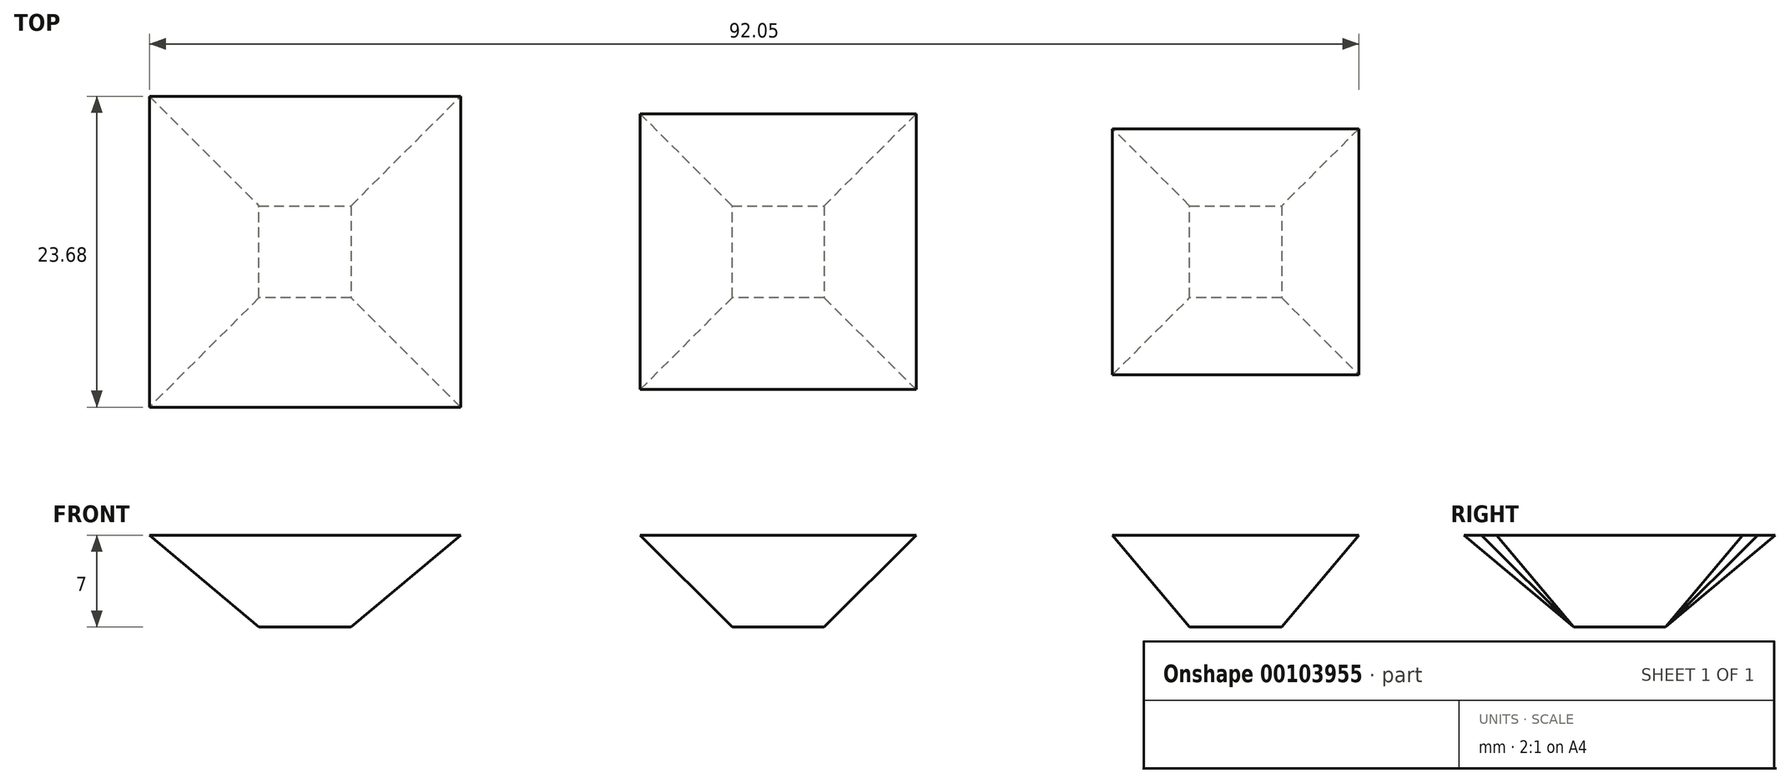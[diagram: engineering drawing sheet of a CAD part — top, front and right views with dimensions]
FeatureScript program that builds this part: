
annotation { "Feature Type Name" : "Feature", "Feature Type Description" : "" }
export const myFeature = defineFeature(function(context is Context, id is Id, definition is map)
    precondition{}
    {
        {
            var Q0;
            Q0=qCreatedBy(makeId("Top.planeOp"),FACE);
            var sketch = newSketch(context, id + "F0", { "sketchPlane" : qUnion([Q0])});
            skLineSegment(sketch, "E0.bottom", {"start": v(3.5, -3.5) * mm, "end": v(-3.5, -3.5) * mm});
            skLineSegment(sketch, "E0.top", {"start": v(3.5, 3.5) * mm, "end": v(-3.5, 3.5) * mm});
            skLineSegment(sketch, "E0.left", {"start": v(3.5, -3.5) * mm, "end": v(3.5, 3.5) * mm});
            skLineSegment(sketch, "E0.right", {"start": v(-3.5, -3.5) * mm, "end": v(-3.5, 3.5) * mm});
            skPoint(sketch, "E0.middle", {"position": v(0, 0) * mm});
            skSolve(sketch);
        }
        {
            var Q0;
            Q0 = qSketchRegion(id + "F0", true);
            extrude(context, id + "F1", {"entities" : qUnion([Q0]), "depth" : 7 * mm, "hasDraft" : true, "draftAngle" : 45 * degree});
        }
        {
            var Q0;
            Q0=qCreatedBy(makeId("Top.planeOp"),FACE);
            var sketch = newSketch(context, id + "F2", { "sketchPlane" : qUnion([Q0])});
            skLineSegment(sketch, "E1.bottom", {"start": v(-32.5, 3.5) * mm, "end": v(-39.5, 3.5) * mm});
            skLineSegment(sketch, "E1.top", {"start": v(-32.5, -3.5) * mm, "end": v(-39.5, -3.5) * mm});
            skLineSegment(sketch, "E1.left", {"start": v(-32.5, 3.5) * mm, "end": v(-32.5, -3.5) * mm});
            skLineSegment(sketch, "E1.right", {"start": v(-39.5, 3.5) * mm, "end": v(-39.5, -3.5) * mm});
            skPoint(sketch, "E1.middle", {"position": v(-36, 0) * mm});
            skSolve(sketch);
        }
        {
            var Q0;
            Q0 = qSketchRegion(id + "F2", true);
            extrude(context, id + "F3", {"entities" : qUnion([Q0]), "depth" : 7 * mm, "hasDraft" : true, "draftAngle" : 50 * degree});
        }
        {
            var Q0;
            Q0=qCreatedBy(makeId("Top.planeOp"),FACE);
            var sketch = newSketch(context, id + "F4", { "sketchPlane" : qUnion([Q0])});
            skLineSegment(sketch, "E2.bottom", {"start": v(38.32, -3.5) * mm, "end": v(31.32, -3.5) * mm});
            skLineSegment(sketch, "E2.top", {"start": v(38.32, 3.5) * mm, "end": v(31.32, 3.5) * mm});
            skLineSegment(sketch, "E2.left", {"start": v(38.32, -3.5) * mm, "end": v(38.32, 3.5) * mm});
            skLineSegment(sketch, "E2.right", {"start": v(31.32, -3.5) * mm, "end": v(31.32, 3.5) * mm});
            skPoint(sketch, "E2.middle", {"position": v(34.82, 0) * mm});
            skSolve(sketch);
        }
        {
            var Q0;
            Q0 = qSketchRegion(id + "F4", true);
            extrude(context, id + "F5", {"entities" : qUnion([Q0]), "depth" : 7 * mm, "hasDraft" : true, "draftAngle" : 40 * degree});
        }
    });
